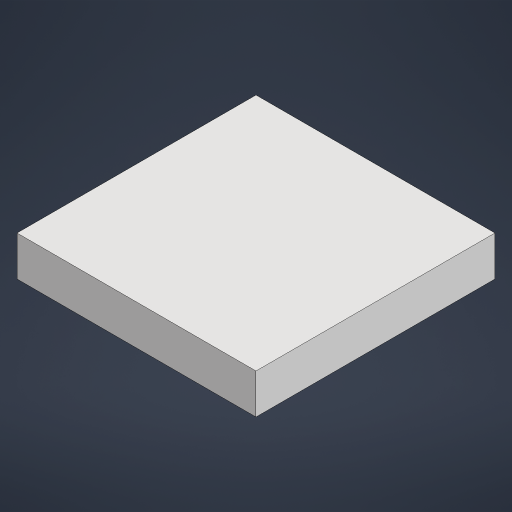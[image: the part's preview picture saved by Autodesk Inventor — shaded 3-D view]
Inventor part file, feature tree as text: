
AUTODESK INVENTOR PART (.ipt)
format: ipt  version: 2023.2 (Build 272271000, 271)  size: 144,896 bytes
history: native  units: in
note: dims shown in document units (in); Inventor stores cm internally (conversion verified against a paired STEP export)
features: extrude x1, sketch x1
ambient origin geometry x8: Origin, YZ Plane, XZ Plane, XY Plane, X Axis, Y Axis, Z Axis, Center Point
bodies: Solid1 (feature_tree)
feature tree (2):
  extrude  "Extrusion1"  Depth=12.0in
  sketch  "Sketch2"  dims[d3=12.0in d4=12.0in d5=2.0in d6=0.0in]
